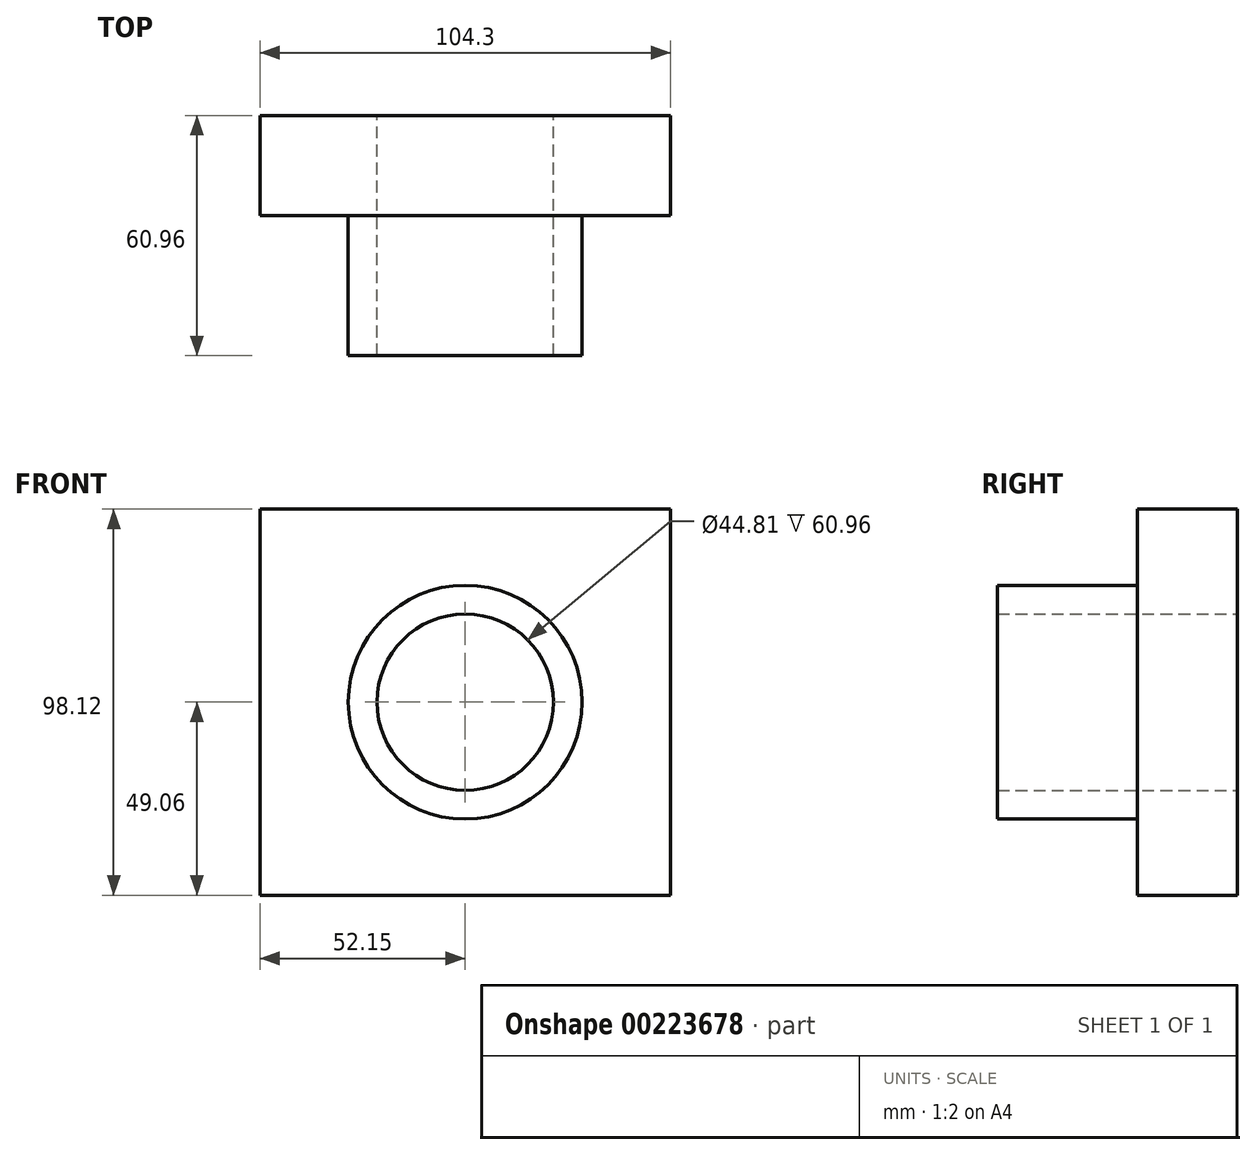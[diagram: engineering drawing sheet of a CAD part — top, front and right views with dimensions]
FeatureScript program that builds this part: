
annotation { "Feature Type Name" : "Feature", "Feature Type Description" : "" }
export const myFeature = defineFeature(function(context is Context, id is Id, definition is map)
    precondition{}
    {
        {
            var Q0;
            Q0=qCreatedBy(makeId("Front.planeOp"),FACE);
            var sketch = newSketch(context, id + "F0", { "sketchPlane" : qUnion([Q0])});
            skLineSegment(sketch, "E0.bottom", {"start": v(-52.15, 49.06) * mm, "end": v(52.15, 49.06) * mm});
            skLineSegment(sketch, "E0.top", {"start": v(-52.15, -49.06) * mm, "end": v(52.15, -49.06) * mm});
            skLineSegment(sketch, "E0.left", {"start": v(-52.15, 49.06) * mm, "end": v(-52.15, -49.06) * mm});
            skLineSegment(sketch, "E0.right", {"start": v(52.15, 49.06) * mm, "end": v(52.15, -49.06) * mm});
            skPoint(sketch, "E0.middle", {"position": v(0, 0) * mm});
            skCircle(sketch, "E1", {"center": v(0, 0) * mm, "radius": 22.4 * mm});
            skSolve(sketch);
        }
        {
            var Q0;
            Q0=makeQuery(id+"F0.imprint","IMPRINT",FACE,{"disambiguationData":[TD([[makeQuery(id+"F0.imprint","IMPRINT",EDGE,{"derivedFrom":sQuery(id+"F0.wireOp",EDGE,"E0.bottom")}),-1.0]])]});
            extrude(context, id + "F1", {"entities" : qUnion([Q0]), "depth" : 25.4 * mm});
        }
        {
            var Q0;
            Q0=makeQuery(id+"F1.opExtrude","CAP_FACE",FACE,{"disambiguationData":[OSD([sQuery(id+"F0.wireOp",EDGE,"E0.bottom"),sQuery(id+"F0.wireOp",EDGE,"E0.top"),sQuery(id+"F0.wireOp",EDGE,"E0.left"),sQuery(id+"F0.wireOp",EDGE,"E0.right"),sQuery(id+"F0.wireOp",EDGE,"E1")])],"isStart":false});
            var sketch = newSketch(context, id + "F2", { "sketchPlane" : qUnion([Q0])});
            skCircle(sketch, "E2", {"center": v(0, 0) * mm, "radius": 29.7 * mm});
            skSolve(sketch);
        }
        {
            var Q0;
            Q0=makeQuery(id+"F2.imprint","IMPRINT",FACE,{"disambiguationData":[TD([[makeQuery(id+"F2.imprint","IMPRINT",EDGE,{"derivedFrom":sQuery(id+"F2.wireOp",EDGE,"E2")}),1.0]])]});
            extrude(context, id + "F3", {"entities" : qUnion([Q0]), "operationType" : NewBodyOperationType.ADD, "depth" : 35.56 * mm});
        }
    });
